# Revit family: U-LINE-2978DANE840Bxxx
name_source: partatom
category: Leuchten
units: mm (PartAtom-declared; Revit-internal decimal feet)

## family parameters
Basisbauteil = Fläche
Beim Laden mit Abzugskörper schneiden = Nein
Bemaßung runder Anschluss = Durchmesser verwenden
Gemeinsam genutzt = Nein
Lichtquelle = Ja
OmniClass-Nummer = 23.80.70.11
OmniClass-Titel = Luminaries for Internal Lighting
Raumberechnungspunkt = Nein
Teiletyp = Normal

## types (2) — shared parameters
Baugruppenkennzeichen = D5020200
Emissionsform beim Rendern sichtbar = Nein
Farbfilter = 16777215
Farbtemperaturverschiebung bei Dämpfen der Lampe = <Keine Auswahl>
Hersteller = RIDI Leuchten GmbH
Lampe = LED
Neigungswinkel = 90.00°
Scheinlast = 62 VA
URL = www.ridi.de
Von Breite des Rechtecks ausssenden = 2974 mm  [stored 9.75722 ft]
Von Länge des Rechtecks aussenden = 64 mm  [stored 0.209974 ft]
brand = RIDI
conformity mark = CE
electrical safety class = 1
height = 58 mm  [stored 0.190289 ft]
ingress protection (IP) code = IP20
length = 2978 mm
nominal frequency = 50-60Hz
nominal voltage = 230
rated input power = 62
voltage type (AC, DC, UC) = AC
weight = 7,5kg
width = 71 mm  [stored 0.23294 ft]
zero-valued in all types: Vorgabe-Ansicht

## per-type parameters (varying)
| type | Datei für fotometrisches Netz | Modell |
| U-LINE 2978DANE840B/MPS0750 | U-LINE_MPS.IES | 0635805AF |
| U-LINE 2978DANE840B/AO0550 | U-LINE_AO.IES | 0635809AF |

note: column(s) folded — value = type name in every type: product name

note: [stored X ft] marks values corroborated as IEEE doubles in the binary element streams (Revit-internal decimal feet)
